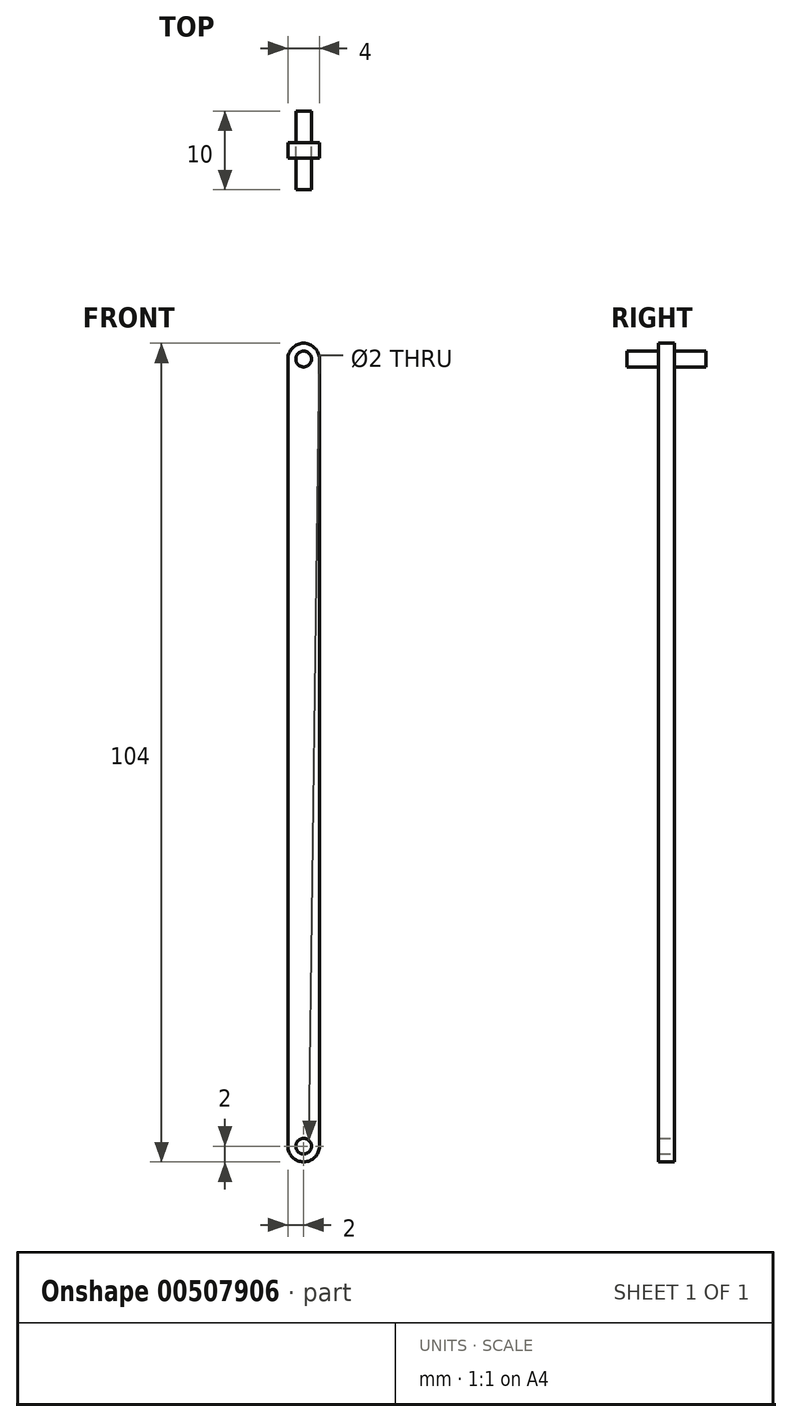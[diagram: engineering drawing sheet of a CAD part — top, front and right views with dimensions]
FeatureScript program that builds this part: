
annotation { "Feature Type Name" : "Feature", "Feature Type Description" : "" }
export const myFeature = defineFeature(function(context is Context, id is Id, definition is map)
    precondition{}
    {
        {
            var Q0;
            Q0=qCreatedBy(makeId("Front.planeOp"),FACE);
            var sketch = newSketch(context, id + "F0", { "sketchPlane" : qUnion([Q0])});
            skCircle(sketch, "E0", {"center": v(0, 0) * mm, "radius": 1 * mm});
            skCircle(sketch, "E1", {"center": v(0, 0) * mm, "radius": 2 * mm});
            skLineSegment(sketch, "E2", {"start": v(0, 0) * mm, "end": v(0, -100) * mm, "construction": true});
            skCircle(sketch, "E3", {"center": v(0, -100) * mm, "radius": 1 * mm});
            skCircle(sketch, "E4", {"center": v(0, -100) * mm, "radius": 2 * mm});
            skLineSegment(sketch, "E5", {"start": v(2, 0) * mm, "end": v(2, -100) * mm});
            skLineSegment(sketch, "E6.MirrorCS", {"start": v(-2, 0) * mm, "end": v(-2, -100) * mm});
            skSolve(sketch);
        }
        {
            var Q0;
            Q0=makeQuery(id+"F0.imprint","IMPRINT",FACE,{"disambiguationData":[TD([[makeQuery(id+"F0.imprint","IMPRINT",EDGE,{"derivedFrom":sQuery(id+"F0.wireOp",EDGE,"E0")}),-1.0]])]});
            var Q1;
            {var subQ0=sQuery(id+"F0.wireOp",EDGE,"E5");Q1=makeQuery(id+"F0.imprint","IMPRINT",FACE,{"disambiguationData":[TD([[makeQuery(id+"F0.imprint","IMPRINT",EDGE,{"derivedFrom":subQ0}),-1.0]])]});}
            var Q2;
            Q2=makeQuery(id+"F0.imprint","IMPRINT",FACE,{"disambiguationData":[TD([[makeQuery(id+"F0.imprint","IMPRINT",EDGE,{"derivedFrom":sQuery(id+"F0.wireOp",EDGE,"E3")}),-1.0]])]});
            extrude(context, id + "F1", {"entities" : qUnion([Q0, Q1, Q2]), "depth" : 2 * mm, "offsetDistance" : 25 * mm, "symmetric" : true});
        }
        {
            var Q0;
            Q0=makeQuery(id+"F0.imprint","IMPRINT",FACE,{"disambiguationData":[TD([[makeQuery(id+"F0.imprint","IMPRINT",EDGE,{"derivedFrom":sQuery(id+"F0.wireOp",EDGE,"E0")}),1.0]])]});
            extrude(context, id + "F2", {"entities" : qUnion([Q0]), "operationType" : NewBodyOperationType.ADD, "depth" : 10 * mm, "offsetDistance" : 25 * mm, "symmetric" : true});
        }
    });
